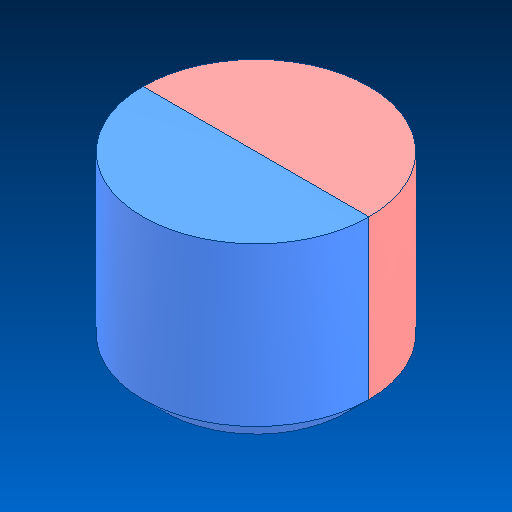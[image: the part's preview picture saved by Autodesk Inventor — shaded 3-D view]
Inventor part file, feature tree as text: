
AUTODESK INVENTOR PART (.ipt)
format: ipt  version: 2022.2 (Build 262287000, 287)  size: 97,792 bytes
history: native  units: in
note: dims shown in document units (in); Inventor stores cm internally (conversion verified against a paired STEP export)
features: chamfer x1
ambient origin geometry x8: Origin, YZ Plane, XZ Plane, XY Plane, X Axis, Y Axis, Z Axis, Center Point
bodies: Solid1 (feature_tree)
feature tree (1):
  chamfer  "Chamfer1"  [1 undecoded]
note: 1 required parameter value undecoded (feature->parameter linkage not recoverable at this tier; creation-order binding heuristic only, values carry confidence <= 0.55)
